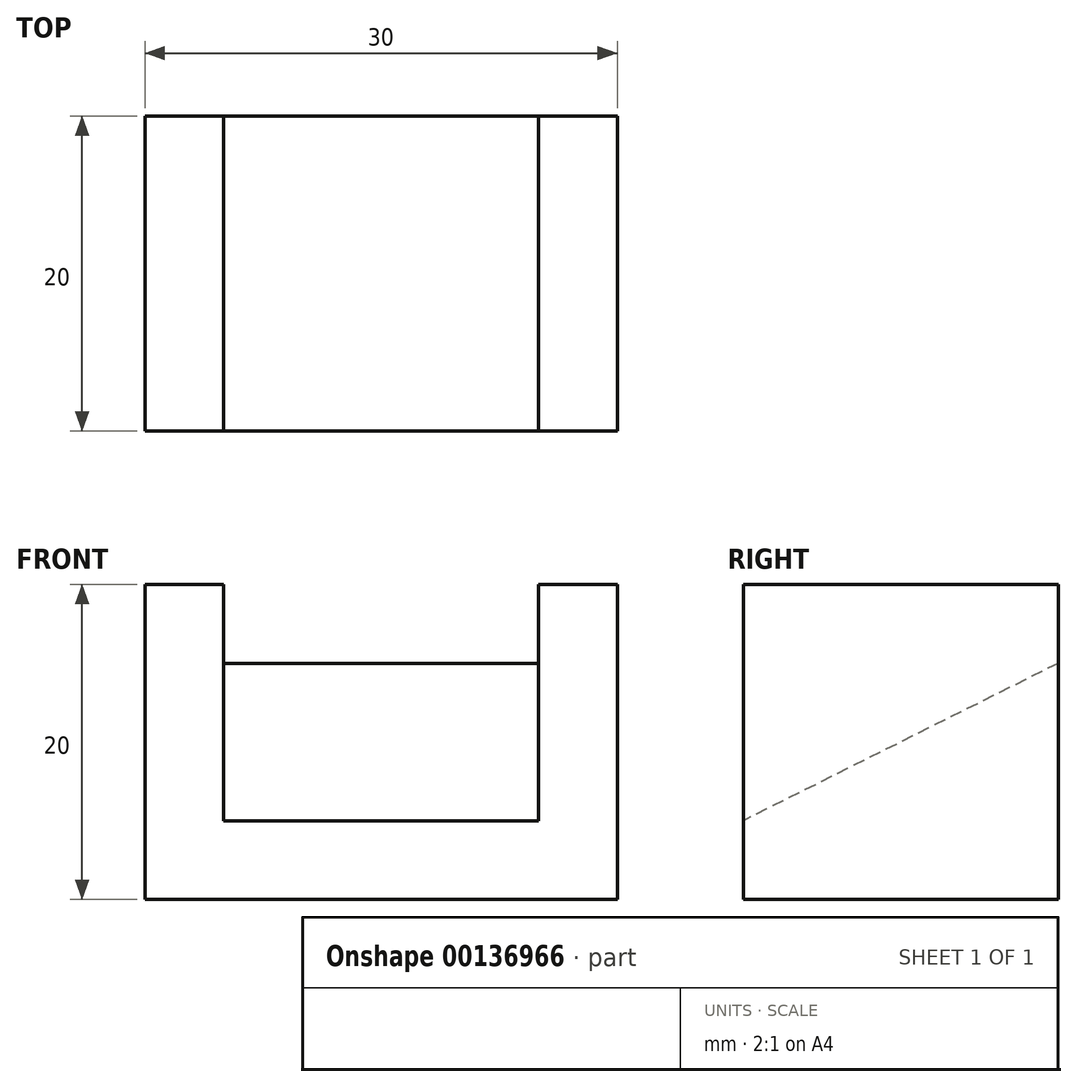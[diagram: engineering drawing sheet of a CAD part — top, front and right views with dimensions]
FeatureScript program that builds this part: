
annotation { "Feature Type Name" : "Feature", "Feature Type Description" : "" }
export const myFeature = defineFeature(function(context is Context, id is Id, definition is map)
    precondition{}
    {
        {
            var Q0;
            Q0=qCreatedBy(makeId("Top.planeOp"),FACE);
            var sketch = newSketch(context, id + "F0", { "sketchPlane" : qUnion([Q0])});
            skLineSegment(sketch, "E0", {"start": v(0, 20) * mm, "end": v(0, 0) * mm});
            skLineSegment(sketch, "E1", {"start": v(0, 0) * mm, "end": v(30, 0) * mm});
            skLineSegment(sketch, "E2", {"start": v(30, 0) * mm, "end": v(30, 20) * mm});
            skLineSegment(sketch, "E3", {"start": v(30, 20) * mm, "end": v(0, 20) * mm});
            skSolve(sketch);
        }
        {
            var Q0;
            Q0 = qSketchRegion(id + "F0", true);
            extrude(context, id + "F1", {"entities" : qUnion([Q0]), "depth" : 20 * mm});
        }
        {
            var Q0;
            Q0=makeQuery(id+"F1.opExtrude","SWEPT_FACE",FACE,{"disambiguationData":[OSD([sQuery(id+"F0.wireOp",EDGE,"E2")])]});
            var sketch = newSketch(context, id + "F2", { "sketchPlane" : qUnion([Q0])});
            skLineSegment(sketch, "E4", {"start": v(20, 20) * mm, "end": v(20, 15) * mm});
            skLineSegment(sketch, "E5", {"start": v(0, 20) * mm, "end": v(20, 20) * mm});
            skLineSegment(sketch, "E6", {"start": v(20, 15) * mm, "end": v(0, 5) * mm});
            skLineSegment(sketch, "E7", {"start": v(0, 5) * mm, "end": v(0, 20) * mm});
            skSolve(sketch);
        }
        {
            var Q0;
            Q0=makeQuery(id+"F2.imprint","IMPRINT",FACE,{"disambiguationData":[TD([[makeQuery(id+"F2.imprint","IMPRINT",EDGE,{"derivedFrom":sQuery(id+"F2.wireOp",EDGE,"E4")}),-1.0]])]});
            extrude(context, id + "F3", {"entities" : qUnion([Q0]), "operationType" : NewBodyOperationType.REMOVE, "oppositeDirection" : true, "depth" : 25 * mm, "hasSecondDirection" : true, "secondDirectionOppositeDirection" : true, "secondDirectionDepth" : 5 * mm});
        }
    });
